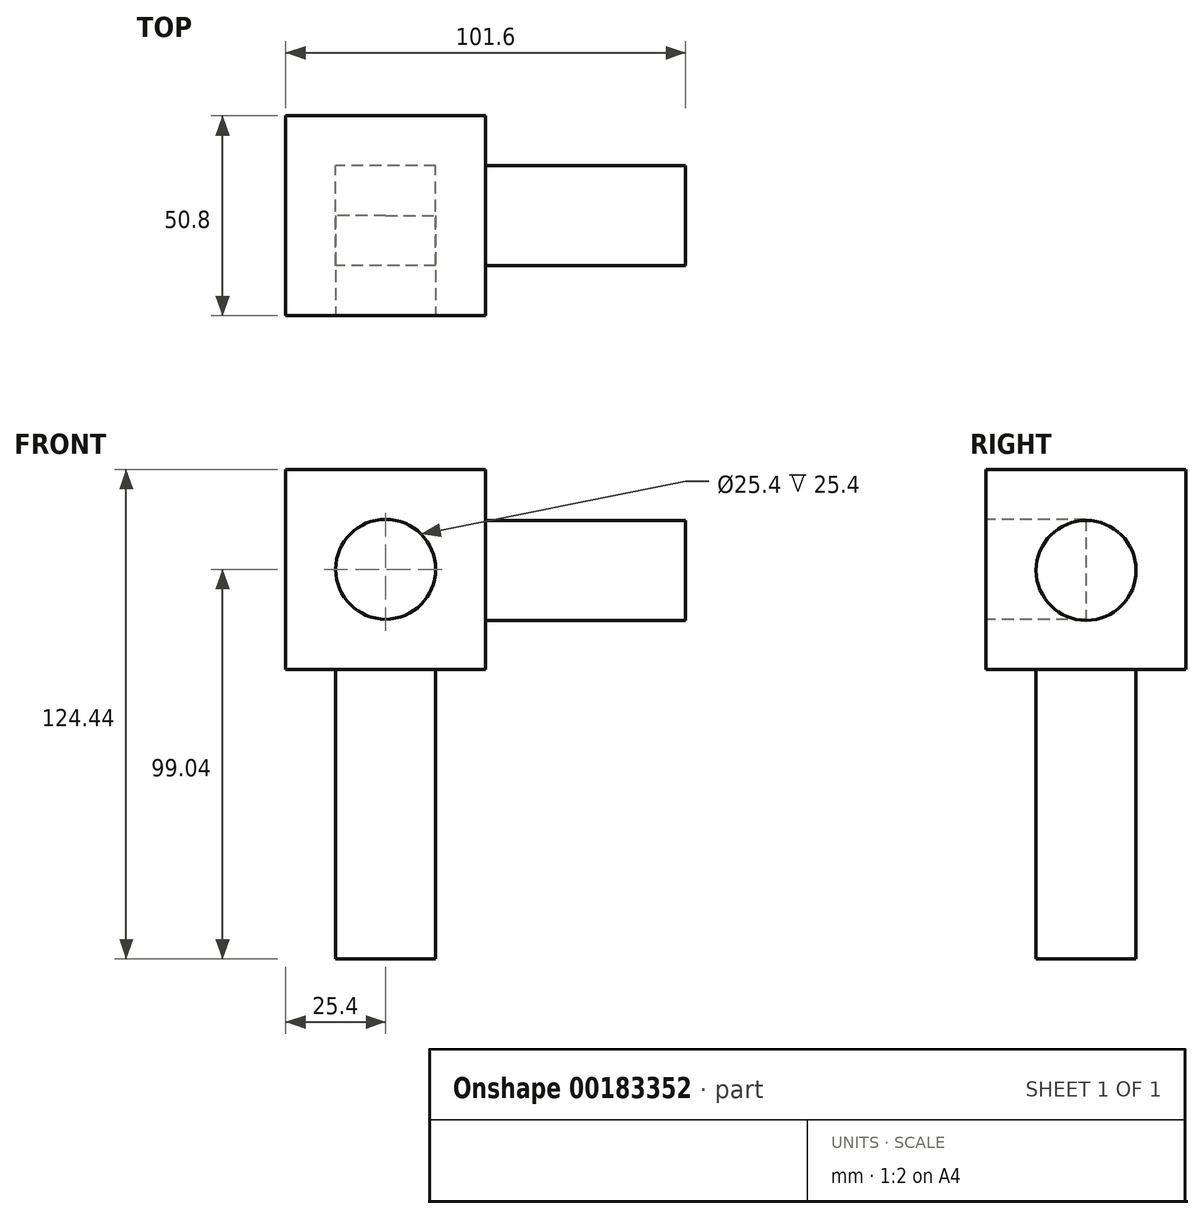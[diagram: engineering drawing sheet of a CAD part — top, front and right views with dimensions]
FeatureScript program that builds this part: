
annotation { "Feature Type Name" : "Feature", "Feature Type Description" : "" }
export const myFeature = defineFeature(function(context is Context, id is Id, definition is map)
    precondition{}
    {
        {
            var Q0;
            Q0=qCreatedBy(makeId("Top.planeOp"),FACE);
            var sketch = newSketch(context, id + "F0", { "sketchPlane" : qUnion([Q0])});
            skLineSegment(sketch, "E0.bottom", {"start": v(-25.4, -25.4) * mm, "end": v(25.4, -25.4) * mm});
            skLineSegment(sketch, "E0.top", {"start": v(-25.4, 25.4) * mm, "end": v(25.4, 25.4) * mm});
            skLineSegment(sketch, "E0.left", {"start": v(-25.4, -25.4) * mm, "end": v(-25.4, 25.4) * mm});
            skLineSegment(sketch, "E0.right", {"start": v(25.4, -25.4) * mm, "end": v(25.4, 25.4) * mm});
            skPoint(sketch, "E0.middle", {"position": v(0, 0) * mm});
            skSolve(sketch);
        }
        {
            var Q0;
            Q0 = qSketchRegion(id + "F0", true);
            extrude(context, id + "F1", {"entities" : qUnion([Q0]), "depth" : 50.8 * mm});
        }
        {
            var Q0;
            Q0=makeQuery(id+"F1.opExtrude","SWEPT_FACE",FACE,{"disambiguationData":[OSD([sQuery(id+"F0.wireOp",EDGE,"E0.right")])]});
            var sketch = newSketch(context, id + "F2", { "sketchPlane" : qUnion([Q0])});
            skCircle(sketch, "E1", {"center": v(0, 25.13) * mm, "radius": 12.7 * mm});
            skSolve(sketch);
        }
        {
            var Q0;
            Q0=makeQuery(id+"F2.imprint","IMPRINT",FACE,{"disambiguationData":[TD([[makeQuery(id+"F2.imprint","IMPRINT",EDGE,{"derivedFrom":sQuery(id+"F2.wireOp",EDGE,"E1")}),1.0]])]});
            extrude(context, id + "F3", {"entities" : qUnion([Q0]), "operationType" : NewBodyOperationType.ADD, "depth" : 50.8 * mm});
        }
        {
            var Q0;
            Q0=makeQuery(id+"F1.opExtrude","CAP_FACE",FACE,{"disambiguationData":[OSD([sQuery(id+"F0.wireOp",EDGE,"E0.bottom"),sQuery(id+"F0.wireOp",EDGE,"E0.top"),sQuery(id+"F0.wireOp",EDGE,"E0.left"),sQuery(id+"F0.wireOp",EDGE,"E0.right")])],"isStart":false});
            var sketch = newSketch(context, id + "F4", { "sketchPlane" : qUnion([Q0])});
            skLineSegment(sketch, "E2.bottom", {"start": v(12.7, -12.7) * mm, "end": v(-12.7, -12.7) * mm});
            skLineSegment(sketch, "E2.top", {"start": v(12.7, 12.7) * mm, "end": v(-12.7, 12.7) * mm});
            skLineSegment(sketch, "E2.left", {"start": v(12.7, -12.7) * mm, "end": v(12.7, 12.7) * mm});
            skLineSegment(sketch, "E2.right", {"start": v(-12.7, -12.7) * mm, "end": v(-12.7, 12.7) * mm});
            skPoint(sketch, "E2.middle", {"position": v(0, 0) * mm});
            skSolve(sketch);
        }
        {
            var Q0;
            Q0=makeQuery(id+"F4.imprint","IMPRINT",FACE,{"disambiguationData":[TD([[makeQuery(id+"F4.imprint","IMPRINT",EDGE,{"derivedFrom":sQuery(id+"F4.wireOp",EDGE,"E2.bottom")}),-1.0]])]});
            extrude(context, id + "F5", {"entities" : qUnion([Q0]), "operationType" : NewBodyOperationType.ADD, "endBound" : BoundingType.THROUGH_ALL, "oppositeDirection" : true, "depth" : 25.4 * mm});
        }
        {
            var Q0;
            Q0=makeQuery(id+"F1.opExtrude","SWEPT_FACE",FACE,{"disambiguationData":[OSD([sQuery(id+"F0.wireOp",EDGE,"E0.bottom")])]});
            var sketch = newSketch(context, id + "F6", { "sketchPlane" : qUnion([Q0])});
            skCircle(sketch, "E3", {"center": v(0, 25.4) * mm, "radius": 12.7 * mm});
            skPoint(sketch, "E3.centerSnap0", {"position": v(-25.4, 25.4) * mm});
            skSolve(sketch);
        }
        {
            var Q0;
            Q0=makeQuery(id+"F6.imprint","IMPRINT",FACE,{"disambiguationData":[TD([[makeQuery(id+"F6.imprint","IMPRINT",EDGE,{"derivedFrom":sQuery(id+"F6.wireOp",EDGE,"E3")}),1.0]])]});
            var Q1;
            Q1=qCreatedBy(makeId("Origin.pointOp"),VERTEX);
            extrude(context, id + "F7", {"entities" : qUnion([Q0]), "operationType" : NewBodyOperationType.REMOVE, "endBound" : BoundingType.UP_TO_VERTEX, "oppositeDirection" : true, "endBoundEntityVertex" : qUnion([Q1]), "depth" : 25.4 * mm});
        }
        {
            var Q0;
            Q0=qCreatedBy(makeId("Top.planeOp"),FACE);
            cPlane(context, id + "F8", {"entities" : qUnion([Q0]), "cplaneType" : CPlaneType.OFFSET, "offset" : 101.6 * mm, "width" : 152.4 * mm, "height" : 152.4 * mm});
        }
    });
